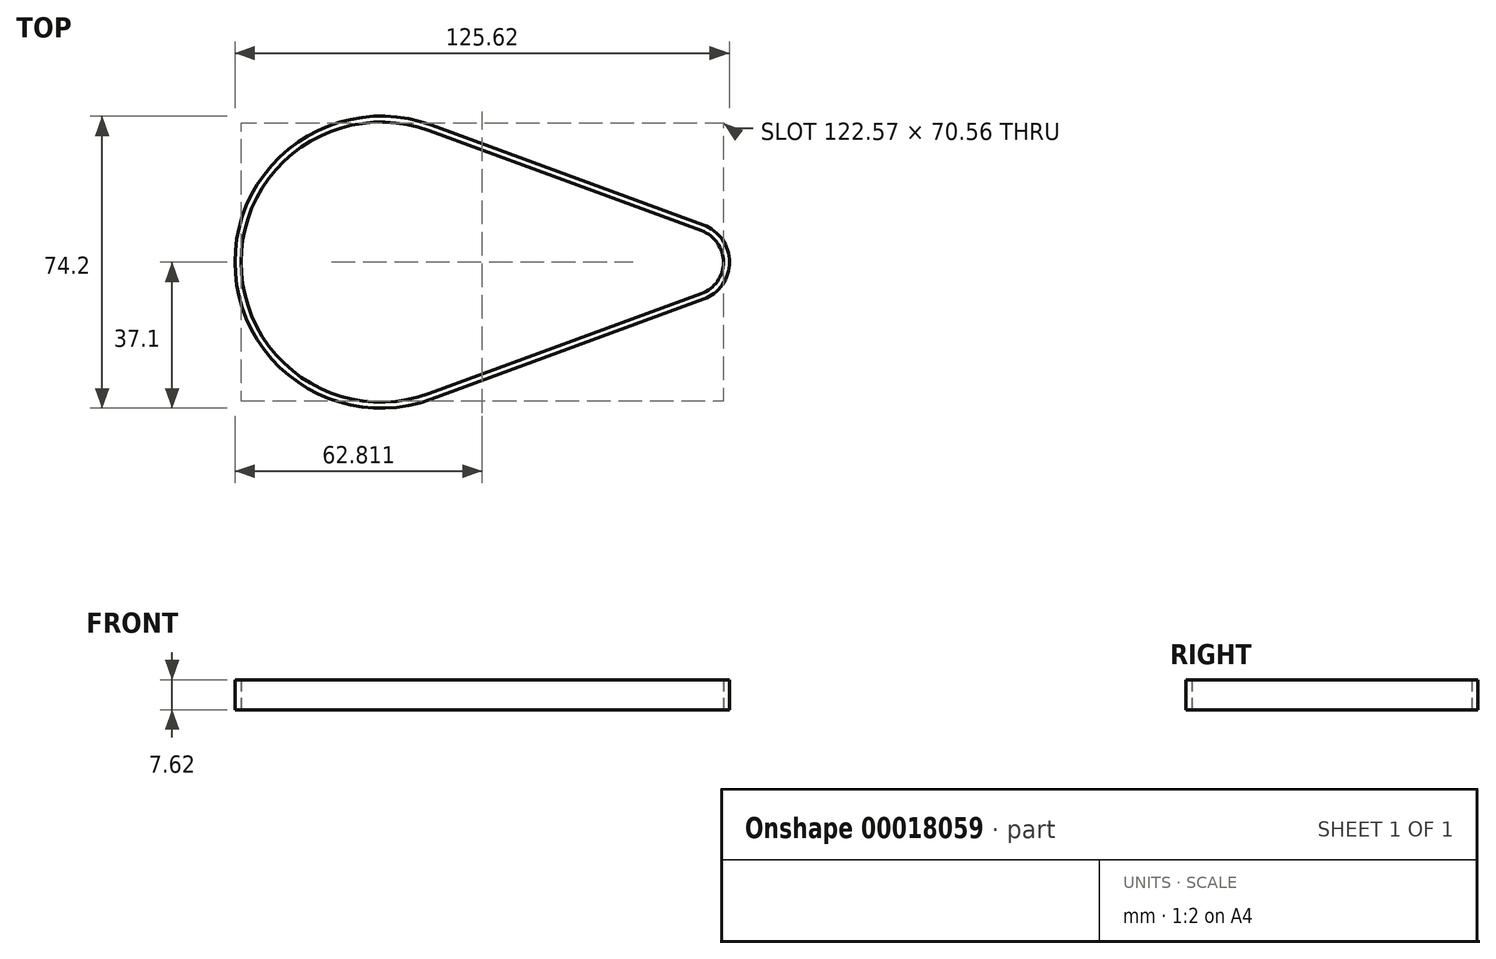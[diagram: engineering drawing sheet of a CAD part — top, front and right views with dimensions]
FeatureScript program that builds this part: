
annotation { "Feature Type Name" : "Feature", "Feature Type Description" : "" }
export const myFeature = defineFeature(function(context is Context, id is Id, definition is map)
    precondition{}
    {
        {
            var Q0;
            Q0=qCreatedBy(makeId("Top.planeOp"),FACE);
            var sketch = newSketch(context, id + "F0", { "sketchPlane" : qUnion([Q0])});
            skArc(sketch, "E0", {"start": v(12.27, 33.4) * mm, "mid": v(-35.57, 0) * mm, "end": v(12.27, -33.4) * mm});
            skArc(sketch, "E1", {"start": v(81.42, -7.99) * mm, "mid": v(87, 0) * mm, "end": v(81.42, 7.99) * mm});
            skLineSegment(sketch, "E2", {"start": v(12.27, 33.4) * mm, "end": v(81.42, 7.99) * mm});
            skLineSegment(sketch, "E3", {"start": v(81.42, -7.99) * mm, "end": v(12.27, -33.4) * mm});
            skSolve(sketch);
        }
        {
            var Q0;
            Q0 = qSketchRegion(id + "F0", true);
            extrude(context, id + "F1", {"entities" : qUnion([Q0]), "depth" : 7.62 * mm});
        }
        {
            var Q0;
            Q0=makeQuery(id+"F1.opExtrude","CAP_FACE",FACE,{"disambiguationData":[OSD([sQuery(id+"F0.wireOp",EDGE,"E0"),sQuery(id+"F0.wireOp",EDGE,"E1"),sQuery(id+"F0.wireOp",EDGE,"E2"),sQuery(id+"F0.wireOp",EDGE,"E3")])],"isStart":false});
            var Q1;
            Q1=makeQuery(id+"F1.opExtrude","CAP_FACE",FACE,{"disambiguationData":[OSD([sQuery(id+"F0.wireOp",EDGE,"E0"),sQuery(id+"F0.wireOp",EDGE,"E1"),sQuery(id+"F0.wireOp",EDGE,"E2"),sQuery(id+"F0.wireOp",EDGE,"E3")])],"isStart":true});
            shell(context, id + "F2", {"entities" : qUnion([Q0, Q1]), "thickness" : 1.52 * mm, "oppositeDirection" : true});
        }
    });
